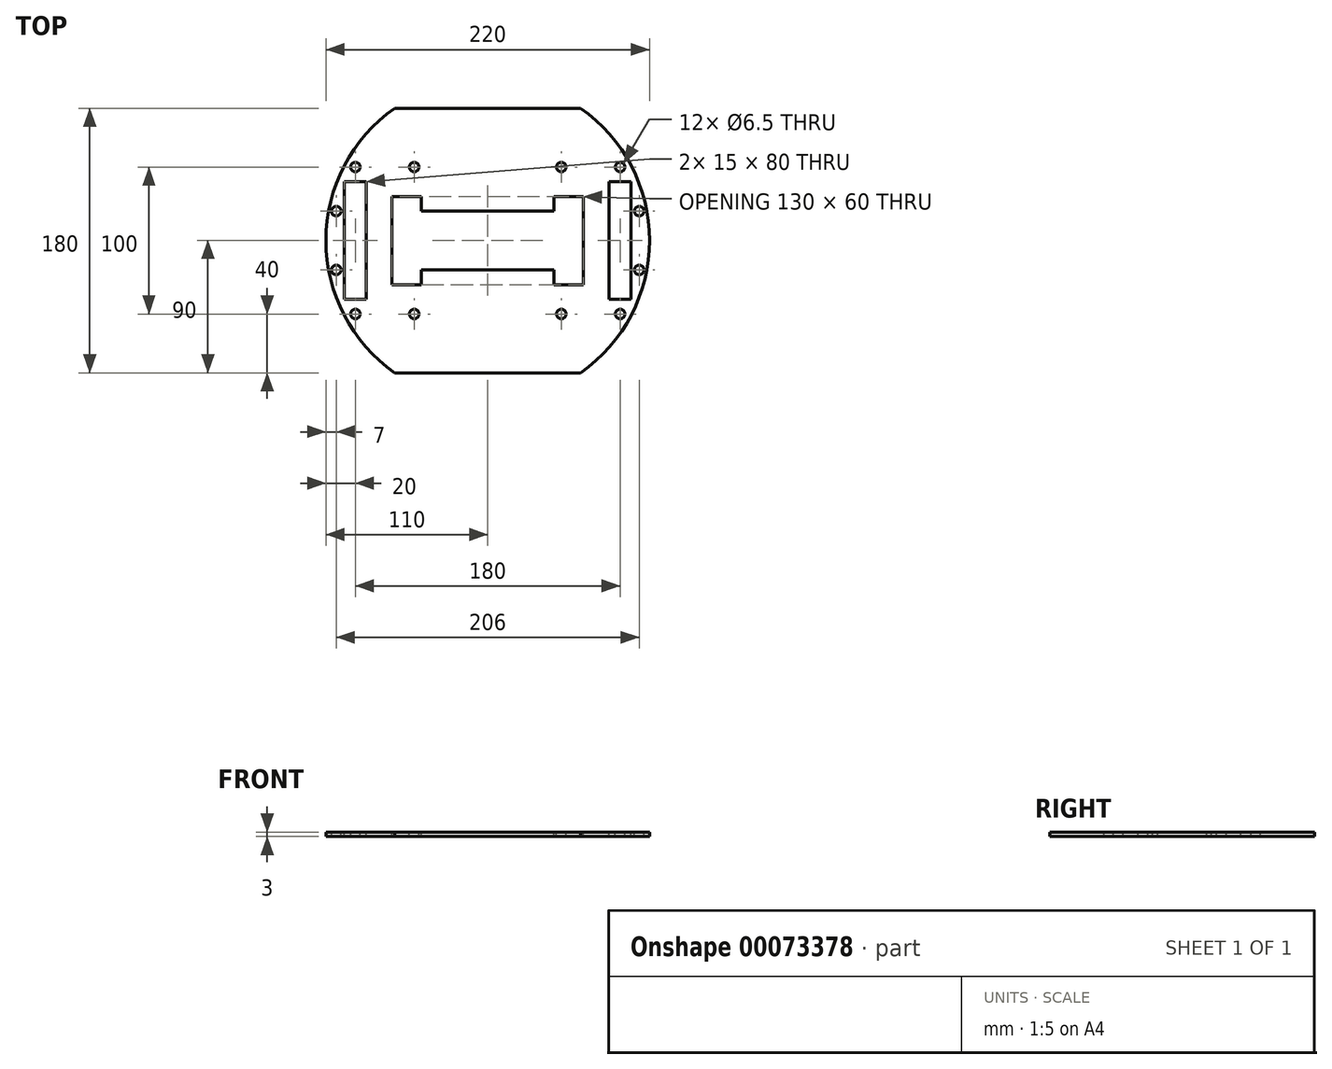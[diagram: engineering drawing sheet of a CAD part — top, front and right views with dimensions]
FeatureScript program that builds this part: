
annotation { "Feature Type Name" : "Feature", "Feature Type Description" : "" }
export const myFeature = defineFeature(function(context is Context, id is Id, definition is map)
    precondition{}
    {
        {
            var Q0;
            Q0=qCreatedBy(makeId("Top.planeOp"),FACE);
            var sketch = newSketch(context, id + "F0", { "sketchPlane" : qUnion([Q0])});
            skCircle(sketch, "E0", {"center": v(0, 0) * mm, "radius": 110 * mm, "construction": true});
            skLineSegment(sketch, "E1.bottom", {"start": v(-63.25, 90) * mm, "end": v(63.25, 90) * mm});
            skLineSegment(sketch, "E1.top", {"start": v(-63.25, -90) * mm, "end": v(63.25, -90) * mm});
            skLineSegment(sketch, "E1.left", {"start": v(-63.25, 90) * mm, "end": v(-63.25, -90) * mm, "construction": true});
            skLineSegment(sketch, "E1.right", {"start": v(63.25, 90) * mm, "end": v(63.25, -90) * mm, "construction": true});
            skArc(sketch, "E2", {"start": v(-63.25, -90) * mm, "mid": v(-110, 0) * mm, "end": v(-63.25, 90) * mm});
            skArc(sketch, "E3", {"start": v(63.25, 90) * mm, "mid": v(110, 0) * mm, "end": v(63.25, -90) * mm});
            skSolve(sketch);
        }
        {
            var Q0;
            Q0=makeQuery(id+"F0.imprint","IMPRINT",FACE,{"disambiguationData":[TD([[makeQuery(id+"F0.imprint","IMPRINT",EDGE,{"derivedFrom":sQuery(id+"F0.wireOp",EDGE,"E1.bottom")}),-1.0]])]});
            extrude(context, id + "F1", {"entities" : qUnion([Q0]), "depth" : 3 * mm, "offsetDistance" : 25 * mm});
        }
        {
            var Q0;
            Q0=makeQuery(id+"F1.opExtrude","CAP_FACE",FACE,{"disambiguationData":[OSD([sQuery(id+"F0.wireOp",EDGE,"E1.bottom"),sQuery(id+"F0.wireOp",EDGE,"E1.top"),sQuery(id+"F0.wireOp",EDGE,"E2"),sQuery(id+"F0.wireOp",EDGE,"E3")])],"isStart":false});
            var sketch = newSketch(context, id + "F2", { "sketchPlane" : qUnion([Q0])});
            skLineSegment(sketch, "E4.bottom", {"start": v(-98, 45) * mm, "end": v(-82, 45) * mm});
            skLineSegment(sketch, "E4.top", {"start": v(-98, -45) * mm, "end": v(-82, -45) * mm});
            skLineSegment(sketch, "E4.left", {"start": v(-98, 45) * mm, "end": v(-98, -45) * mm});
            skLineSegment(sketch, "E4.right", {"start": v(-82, 45) * mm, "end": v(-82, -45) * mm});
            skLineSegment(sketch, "E5.bottom", {"start": v(-95, 45) * mm, "end": v(-85, 45) * mm});
            skLineSegment(sketch, "E5.top", {"start": v(-95, 55) * mm, "end": v(-85, 55) * mm});
            skLineSegment(sketch, "E5.left", {"start": v(-95, 45) * mm, "end": v(-95, 55) * mm});
            skLineSegment(sketch, "E5.right", {"start": v(-85, 45) * mm, "end": v(-85, 55) * mm});
            skLineSegment(sketch, "E6.bottom", {"start": v(-95, -45) * mm, "end": v(-85, -45) * mm});
            skLineSegment(sketch, "E6.top", {"start": v(-95, -55) * mm, "end": v(-85, -55) * mm});
            skLineSegment(sketch, "E6.left", {"start": v(-95, -45) * mm, "end": v(-95, -55) * mm});
            skLineSegment(sketch, "E6.right", {"start": v(-85, -45) * mm, "end": v(-85, -55) * mm});
            skLineSegment(sketch, "E7.bottom", {"start": v(-109, 15) * mm, "end": v(-98, 15) * mm});
            skLineSegment(sketch, "E7.top", {"start": v(-109, -15) * mm, "end": v(-98, -15) * mm});
            skLineSegment(sketch, "E7.left", {"start": v(-109, 15) * mm, "end": v(-109, -15) * mm});
            skLineSegment(sketch, "E7.right", {"start": v(-98, 15) * mm, "end": v(-98, -15) * mm});
            skPoint(sketch, "E8", {"position": v(-98, 0) * mm});
            skPoint(sketch, "E9", {"position": v(-90, 45) * mm});
            skPoint(sketch, "E10", {"position": v(-90, -45) * mm});
            skLineSegment(sketch, "E11.bottom", {"start": v(-98, -15) * mm, "end": v(-108, -15) * mm});
            skLineSegment(sketch, "E11.top", {"start": v(-98, -25) * mm, "end": v(-108, -25) * mm});
            skLineSegment(sketch, "E11.left", {"start": v(-98, -15) * mm, "end": v(-98, -25) * mm});
            skLineSegment(sketch, "E11.right", {"start": v(-108, -15) * mm, "end": v(-108, -25) * mm});
            skLineSegment(sketch, "E12.bottom", {"start": v(-98, 15) * mm, "end": v(-108, 15) * mm});
            skLineSegment(sketch, "E12.top", {"start": v(-98, 25) * mm, "end": v(-108, 25) * mm});
            skLineSegment(sketch, "E12.left", {"start": v(-98, 15) * mm, "end": v(-98, 25) * mm});
            skLineSegment(sketch, "E12.right", {"start": v(-108, 15) * mm, "end": v(-108, 25) * mm});
            skLineSegment(sketch, "E13", {"start": v(-98, -15) * mm, "end": v(-108, -25) * mm});
            skLineSegment(sketch, "E14", {"start": v(-98, 15) * mm, "end": v(-108, 25) * mm});
            skPoint(sketch, "E15", {"position": v(-103, 20) * mm});
            skPoint(sketch, "E16", {"position": v(-103, -20) * mm});
            skLineSegment(sketch, "E17", {"start": v(-85, 45) * mm, "end": v(-95, 55) * mm});
            skLineSegment(sketch, "E18", {"start": v(-85, -45) * mm, "end": v(-95, -55) * mm});
            skPoint(sketch, "E19", {"position": v(-90, -50) * mm});
            skPoint(sketch, "E20", {"position": v(-90, 50) * mm});
            skLineSegment(sketch, "E21.MirrorCS", {"start": v(108, 15) * mm, "end": v(108, 25) * mm});
            skLineSegment(sketch, "E22.MirrorCS", {"start": v(98, 15) * mm, "end": v(98, 25) * mm});
            skLineSegment(sketch, "E23.MirrorCS", {"start": v(98, 15) * mm, "end": v(108, 15) * mm});
            skLineSegment(sketch, "E24.MirrorCS", {"start": v(108, -15) * mm, "end": v(108, -25) * mm});
            skLineSegment(sketch, "E25.MirrorCS", {"start": v(98, -15) * mm, "end": v(108, -15) * mm});
            skLineSegment(sketch, "E26.MirrorCS", {"start": v(98, 25) * mm, "end": v(108, 25) * mm});
            skLineSegment(sketch, "E27.MirrorCS", {"start": v(85, -45) * mm, "end": v(95, -55) * mm});
            skLineSegment(sketch, "E28.MirrorCS", {"start": v(95, -45) * mm, "end": v(85, -45) * mm});
            skLineSegment(sketch, "E29.MirrorCS", {"start": v(95, -55) * mm, "end": v(85, -55) * mm});
            skLineSegment(sketch, "E30.MirrorCS", {"start": v(95, -45) * mm, "end": v(95, -55) * mm});
            skLineSegment(sketch, "E31.MirrorCS", {"start": v(98, -15) * mm, "end": v(108, -25) * mm});
            skLineSegment(sketch, "E32.MirrorCS", {"start": v(98, 15) * mm, "end": v(108, 25) * mm});
            skLineSegment(sketch, "E33.MirrorCS", {"start": v(98, -15) * mm, "end": v(98, -25) * mm});
            skLineSegment(sketch, "E34.MirrorCS", {"start": v(85, -45) * mm, "end": v(85, -55) * mm});
            skLineSegment(sketch, "E35.MirrorCS", {"start": v(98, -25) * mm, "end": v(108, -25) * mm});
            skLineSegment(sketch, "E36.MirrorCS", {"start": v(98, 45) * mm, "end": v(82, 45) * mm});
            skLineSegment(sketch, "E37.MirrorCS", {"start": v(109, -15) * mm, "end": v(98, -15) * mm});
            skLineSegment(sketch, "E38.MirrorCS", {"start": v(98, -45) * mm, "end": v(82, -45) * mm});
            skLineSegment(sketch, "E39.MirrorCS", {"start": v(109, 15) * mm, "end": v(98, 15) * mm});
            skLineSegment(sketch, "E40.MirrorCS", {"start": v(95, 45) * mm, "end": v(95, 55) * mm});
            skLineSegment(sketch, "E41.MirrorCS", {"start": v(95, 45) * mm, "end": v(85, 45) * mm});
            skPoint(sketch, "E42.MirrorP", {"position": v(103, -20) * mm});
            skPoint(sketch, "E43.MirrorP", {"position": v(103, 20) * mm});
            skPoint(sketch, "E44.MirrorP", {"position": v(90, -50) * mm});
            skPoint(sketch, "E45.MirrorP", {"position": v(98, 0) * mm});
            skLineSegment(sketch, "E46.MirrorCS", {"start": v(85, 45) * mm, "end": v(95, 55) * mm});
            skLineSegment(sketch, "E47.MirrorCS", {"start": v(95, 55) * mm, "end": v(85, 55) * mm});
            skPoint(sketch, "E48.MirrorP", {"position": v(90, -45) * mm});
            skLineSegment(sketch, "E49.MirrorCS", {"start": v(98, 15) * mm, "end": v(98, -15) * mm});
            skPoint(sketch, "E50.MirrorP", {"position": v(90, 45) * mm});
            skPoint(sketch, "E51.MirrorP", {"position": v(90, 50) * mm});
            skLineSegment(sketch, "E52.MirrorCS", {"start": v(82, 45) * mm, "end": v(82, -45) * mm});
            skLineSegment(sketch, "E53.MirrorCS", {"start": v(109, 15) * mm, "end": v(109, -15) * mm});
            skLineSegment(sketch, "E54.MirrorCS", {"start": v(85, 45) * mm, "end": v(85, 55) * mm});
            skLineSegment(sketch, "E55.MirrorCS", {"start": v(98, 45) * mm, "end": v(98, -45) * mm});
            skSolve(sketch);
        }
        {
            var Q0;
            Q0=sQuery(id+"F2.wireOp",VERTEX,"f939c1bc-4f0a-46cc-9fde-5168f060ff73");
            var Q1;
            Q1=sQuery(id+"F2.wireOp",VERTEX,"E15");
            var Q2;
            Q2=sQuery(id+"F2.wireOp",VERTEX,"E16");
            var Q3;
            Q3=sQuery(id+"F2.wireOp",VERTEX,"12f0103e-799c-4177-9ba6-3f1d33425432");
            var Q4;
            Q4=sQuery(id+"F2.wireOp",VERTEX,"2fcbc748-485c-401b-9c6b-515daa93bae028.MirrorP");
            var Q5;
            Q5=sQuery(id+"F2.wireOp",VERTEX,"2fcbc748-485c-401b-9c6b-515daa93bae018.MirrorP");
            var Q6;
            Q6=sQuery(id+"F2.wireOp",VERTEX,"2fcbc748-485c-401b-9c6b-515daa93bae030.MirrorP");
            var Q7;
            Q7=sQuery(id+"F2.wireOp",VERTEX,"2fcbc748-485c-401b-9c6b-515daa93bae022.MirrorP");
            var Q8;
            Q8=sQuery(id+"F2.wireOp",VERTEX,"E20");
            var Q9;
            Q9=sQuery(id+"F2.wireOp",VERTEX,"E19");
            var Q10;
            Q10=sQuery(id+"F2.wireOp",VERTEX,"E44.MirrorP");
            var Q11;
            Q11=sQuery(id+"F2.wireOp",VERTEX,"E51.MirrorP");
            var Q12;
            Q12=sQuery(id+"F2.wireOp",VERTEX,"E43.MirrorP");
            var Q13;
            Q13=sQuery(id+"F2.wireOp",VERTEX,"E42.MirrorP");
            var Q14;
            Q14=makeQuery(id+"F1.opExtrude","SWEPT_BODY",BODY,{"disambiguationData":[OSD([sQuery(id+"F0.wireOp",EDGE,"E1.bottom"),sQuery(id+"F0.wireOp",EDGE,"E1.top"),sQuery(id+"F0.wireOp",EDGE,"E2"),sQuery(id+"F0.wireOp",EDGE,"E3")])]});
            hole(context, id + "F3", {"style" : HoleStyle.SIMPLE, "endStyle" : HoleEndStyle.THROUGH, "holeDiameter" : 6.5 * mm, "majorDiameter" : 5 * mm, "tappedDepth" : 12 * mm, "tapClearance" : 3, "locations" : qUnion([Q0, Q1, Q2, Q3, Q4, Q5, Q6, Q7, Q8, Q9, Q10, Q11, Q12, Q13]), "scope" : qUnion([Q14])});
        }
        {
            var Q0;
            Q0=makeQuery(id+"F1.opExtrude","CAP_FACE",FACE,{"disambiguationData":[OSD([sQuery(id+"F0.wireOp",EDGE,"E1.bottom"),sQuery(id+"F0.wireOp",EDGE,"E1.top"),sQuery(id+"F0.wireOp",EDGE,"E2"),sQuery(id+"F0.wireOp",EDGE,"E3")])],"isStart":false});
            var sketch = newSketch(context, id + "F4", { "sketchPlane" : qUnion([Q0])});
            skLineSegment(sketch, "E56.bottom", {"start": v(-50, 50) * mm, "end": v(50, 50) * mm});
            skLineSegment(sketch, "E56.top", {"start": v(-50, -50) * mm, "end": v(50, -50) * mm});
            skLineSegment(sketch, "E56.left", {"start": v(-50, 50) * mm, "end": v(-50, -50) * mm});
            skLineSegment(sketch, "E56.right", {"start": v(50, 50) * mm, "end": v(50, -50) * mm});
            skLineSegment(sketch, "E57", {"start": v(-50, 50) * mm, "end": v(50, -50) * mm, "construction": true});
            skPoint(sketch, "E58", {"position": v(0, 0) * mm});
            skSolve(sketch);
        }
        {
            var Q0;
            Q0=sQuery(id+"F4.wireOp",VERTEX,"E56.bottom.start");
            var Q1;
            Q1=sQuery(id+"F4.wireOp",VERTEX,"E56.bottom.end");
            var Q2;
            Q2=sQuery(id+"F4.wireOp",VERTEX,"E56.top.end");
            var Q3;
            Q3=sQuery(id+"F4.wireOp",VERTEX,"E56.top.start");
            var Q4;
            Q4=makeQuery(id+"F1.opExtrude","SWEPT_BODY",BODY,{"disambiguationData":[OSD([sQuery(id+"F0.wireOp",EDGE,"E1.bottom"),sQuery(id+"F0.wireOp",EDGE,"E1.top"),sQuery(id+"F0.wireOp",EDGE,"E2"),sQuery(id+"F0.wireOp",EDGE,"E3")])]});
            hole(context, id + "F5", {"style" : HoleStyle.SIMPLE, "endStyle" : HoleEndStyle.THROUGH, "holeDiameter" : 6.5 * mm, "majorDiameter" : 5 * mm, "tappedDepth" : 12 * mm, "tapClearance" : 3, "locations" : qUnion([Q0, Q1, Q2, Q3]), "scope" : qUnion([Q4])});
        }
        {
            var Q0;
            Q0=makeQuery(id+"F1.opExtrude","CAP_FACE",FACE,{"disambiguationData":[OSD([sQuery(id+"F0.wireOp",EDGE,"E1.bottom"),sQuery(id+"F0.wireOp",EDGE,"E1.top"),sQuery(id+"F0.wireOp",EDGE,"E2"),sQuery(id+"F0.wireOp",EDGE,"E3")])],"isStart":false});
            var sketch = newSketch(context, id + "F6", { "sketchPlane" : qUnion([Q0])});
            skLineSegment(sketch, "E59.bottom", {"start": v(-45, 20) * mm, "end": v(45, 20) * mm});
            skLineSegment(sketch, "E59.top", {"start": v(-45, -20) * mm, "end": v(45, -20) * mm});
            skLineSegment(sketch, "E59.left", {"start": v(-45, 20) * mm, "end": v(-45, -20) * mm});
            skLineSegment(sketch, "E59.right", {"start": v(45, 20) * mm, "end": v(45, -20) * mm});
            skLineSegment(sketch, "E60", {"start": v(-45, 20) * mm, "end": v(45, -20) * mm, "construction": true});
            skPoint(sketch, "E61", {"position": v(0, 0) * mm});
            skPoint(sketch, "E62", {"position": v(-45, 0) * mm});
            skPoint(sketch, "E63", {"position": v(45, 0) * mm});
            skLineSegment(sketch, "E64.bottom", {"start": v(-65, 30) * mm, "end": v(-45, 30) * mm});
            skLineSegment(sketch, "E64.top", {"start": v(-65, -30) * mm, "end": v(-45, -30) * mm});
            skLineSegment(sketch, "E64.left", {"start": v(-65, 30) * mm, "end": v(-65, -30) * mm});
            skLineSegment(sketch, "E64.right", {"start": v(-45, 30) * mm, "end": v(-45, -30) * mm});
            skLineSegment(sketch, "E65.bottom", {"start": v(65, 30) * mm, "end": v(45, 30) * mm});
            skLineSegment(sketch, "E65.top", {"start": v(65, -30) * mm, "end": v(45, -30) * mm});
            skLineSegment(sketch, "E65.left", {"start": v(65, 30) * mm, "end": v(65, -30) * mm});
            skLineSegment(sketch, "E65.right", {"start": v(45, 30) * mm, "end": v(45, -30) * mm});
            skSolve(sketch);
        }
        {
            var Q0;
            {var subQ2=sQuery(id+"F6.wireOp",EDGE,"E64.bottom");Q0=makeQuery(id+"F6.imprint","IMPRINT",FACE,{"disambiguationData":[TD([[makeQuery(id+"F6.imprint","IMPRINT",EDGE,{"derivedFrom":subQ2}),-1.0]])]});}
            var Q1;
            {var subQ0=sQuery(id+"F6.wireOp",EDGE,"E59.bottom");Q1=makeQuery(id+"F6.imprint","IMPRINT",FACE,{"disambiguationData":[TD([[makeQuery(id+"F6.imprint","IMPRINT",EDGE,{"derivedFrom":subQ0}),-1.0]])]});}
            var Q2;
            {var subQ2=sQuery(id+"F6.wireOp",EDGE,"E65.bottom");Q2=makeQuery(id+"F6.imprint","IMPRINT",FACE,{"disambiguationData":[TD([[makeQuery(id+"F6.imprint","IMPRINT",EDGE,{"derivedFrom":subQ2}),1.0]])]});}
            extrude(context, id + "F7", {"entities" : qUnion([Q0, Q1, Q2]), "operationType" : NewBodyOperationType.REMOVE, "endBound" : BoundingType.THROUGH_ALL, "oppositeDirection" : true, "depth" : 25 * mm, "offsetDistance" : 25 * mm});
        }
        {
            var Q0;
            Q0=makeQuery(id+"F1.opExtrude","CAP_FACE",FACE,{"disambiguationData":[OSD([sQuery(id+"F0.wireOp",EDGE,"E1.bottom"),sQuery(id+"F0.wireOp",EDGE,"E1.top"),sQuery(id+"F0.wireOp",EDGE,"E2"),sQuery(id+"F0.wireOp",EDGE,"E3")])],"isStart":false});
            var sketch = newSketch(context, id + "F8", { "sketchPlane" : qUnion([Q0])});
            skLineSegment(sketch, "E66.bottom", {"start": v(-97.5, 40) * mm, "end": v(-82.5, 40) * mm});
            skLineSegment(sketch, "E66.top", {"start": v(-97.5, -40) * mm, "end": v(-82.5, -40) * mm});
            skLineSegment(sketch, "E66.left", {"start": v(-97.5, 40) * mm, "end": v(-97.5, -40) * mm});
            skLineSegment(sketch, "E66.right", {"start": v(-82.5, 40) * mm, "end": v(-82.5, -40) * mm});
            skLineSegment(sketch, "E67.bottom", {"start": v(82.5, 40) * mm, "end": v(97.5, 40) * mm});
            skLineSegment(sketch, "E67.top", {"start": v(82.5, -40) * mm, "end": v(97.5, -40) * mm});
            skLineSegment(sketch, "E67.left", {"start": v(82.5, 40) * mm, "end": v(82.5, -40) * mm});
            skLineSegment(sketch, "E67.right", {"start": v(97.5, 40) * mm, "end": v(97.5, -40) * mm});
            skPoint(sketch, "E68", {"position": v(-82.5, 0) * mm});
            skPoint(sketch, "E69", {"position": v(82.5, 0) * mm});
            skLineSegment(sketch, "E70", {"start": v(90, 40) * mm, "end": v(90, 50) * mm});
            skLineSegment(sketch, "E71", {"start": v(-90, 40) * mm, "end": v(-90, 50) * mm});
            skSolve(sketch);
        }
        {
            var Q0;
            Q0=makeQuery(id+"F8.imprint","IMPRINT",FACE,{"disambiguationData":[TD([[makeQuery(id+"F8.imprint","IMPRINT",EDGE,{"derivedFrom":sQuery(id+"F8.wireOp",EDGE,"E66.top")}),1.0]])]});
            var Q1;
            Q1=makeQuery(id+"F8.imprint","IMPRINT",FACE,{"disambiguationData":[TD([[makeQuery(id+"F8.imprint","IMPRINT",EDGE,{"derivedFrom":sQuery(id+"F8.wireOp",EDGE,"E67.top")}),1.0]])]});
            extrude(context, id + "F9", {"entities" : qUnion([Q0, Q1]), "operationType" : NewBodyOperationType.REMOVE, "endBound" : BoundingType.THROUGH_ALL, "oppositeDirection" : true, "depth" : 25 * mm, "offsetDistance" : 25 * mm});
        }
    });
